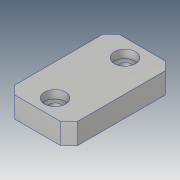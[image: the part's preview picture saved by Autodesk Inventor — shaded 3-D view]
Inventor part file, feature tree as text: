
AUTODESK INVENTOR PART (.ipt)
format: ipt  version: 2018.2 (Build 222227000, 227)  size: 107,008 bytes
history: native  units: mm
features: sketch x3, other x1, extrude x1, hole x1, chamfer x1
ambient origin geometry x8: Origin, YZ Plane, XZ Plane, XY Plane, X Axis, Y Axis, Z Axis, Center Point
bodies: Volumenkörper1 (feature_tree)
feature tree (7):
  other  "200-50-WHEEL-CONNECTOR-30MM-01.ipt"
  extrude  "Grundkörper"  Depth=10.0mm TaperAngle=0.0deg
  hole  "DIN7984_M5_Boh"  [1 undecoded]
  chamfer  "Fase1"  [1 undecoded]
  sketch  "Skizze"
  sketch  "Skizze2"  dims[d0=10.0mm d1=10.0mm d2=0.0mm]
  sketch  "Skizze3"  dims[d3=5.5mm d4=6.0mm d5=10.0mm d6=3.9mm d7=90.0deg d8=8.0mm d9=20.594885mm d10=4.0mm d11=2.0mm d12=45.0deg]
note: 2 required parameter values undecoded (feature->parameter linkage not recoverable at this tier; creation-order binding heuristic only, values carry confidence <= 0.55)
